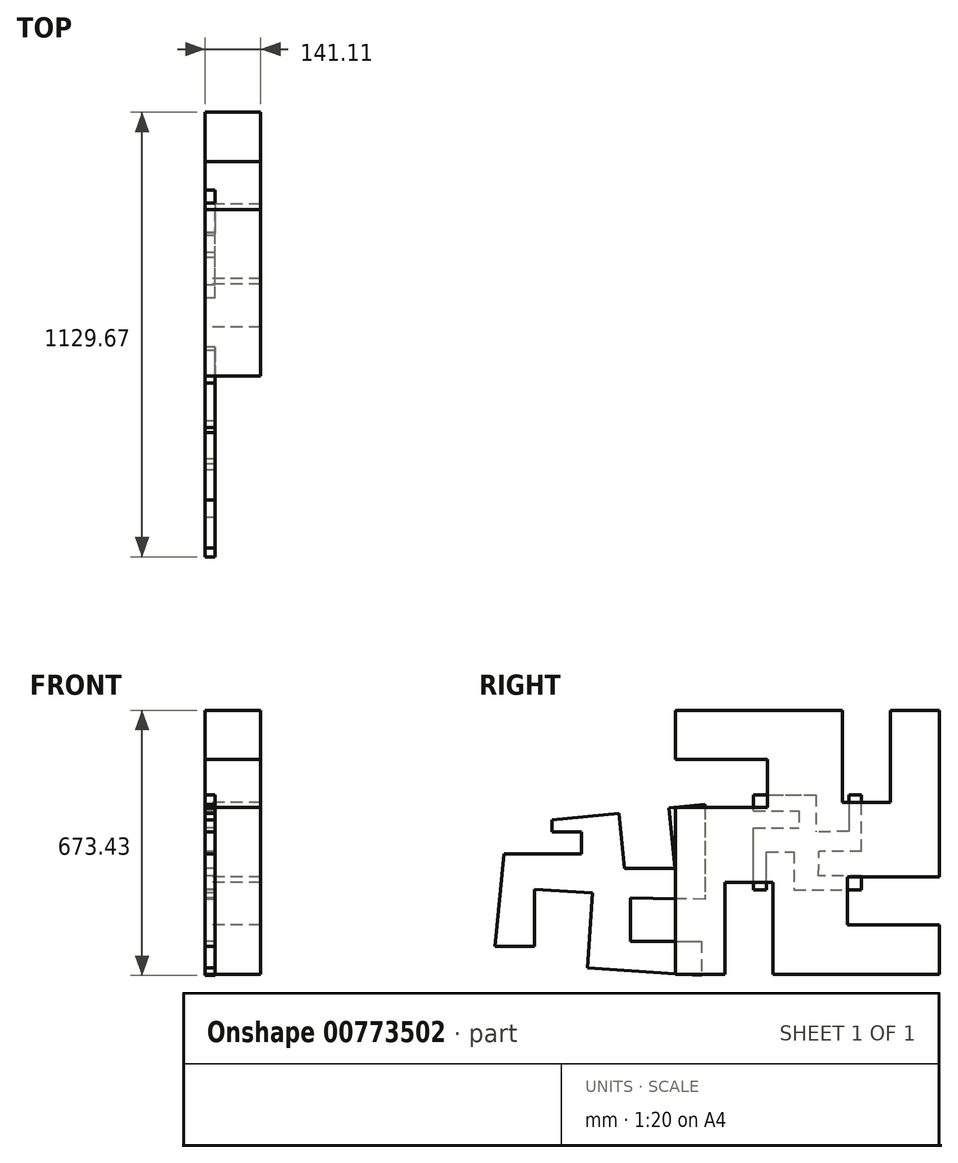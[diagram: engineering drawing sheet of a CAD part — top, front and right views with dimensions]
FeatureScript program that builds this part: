
annotation { "Feature Type Name" : "Feature", "Feature Type Description" : "" }
export const myFeature = defineFeature(function(context is Context, id is Id, definition is map)
    precondition{}
    {
        {
            var Q0;
            Q0=qCreatedBy(makeId("Right.planeOp"),FACE);
            var sketch = newSketch(context, id + "F0", { "sketchPlane" : qUnion([Q0])});
            skLineSegment(sketch, "E0.bottom", {"start": v(-137.35, -120.87) * mm, "end": v(137.35, -120.87) * mm});
            skLineSegment(sketch, "E0.top", {"start": v(-137.35, 120.87) * mm, "end": v(137.35, 120.87) * mm});
            skLineSegment(sketch, "E0.left", {"start": v(-137.35, -120.87) * mm, "end": v(-137.35, 120.87) * mm});
            skLineSegment(sketch, "E0.right", {"start": v(137.35, -120.87) * mm, "end": v(137.35, 120.87) * mm});
            skPoint(sketch, "E0.middle", {"position": v(0, 0) * mm});
            skLineSegment(sketch, "E1", {"start": v(-137.35, 79.77) * mm, "end": v(-21.68, 79.77) * mm});
            skLineSegment(sketch, "E2", {"start": v(21.28, 120.87) * mm, "end": v(21.28, 26.6) * mm});
            skLineSegment(sketch, "E3", {"start": v(104.57, 120.87) * mm, "end": v(104.57, 27.18) * mm});
            skLineSegment(sketch, "E4", {"start": v(104.57, 27.18) * mm, "end": v(21.28, 26.6) * mm});
            skLineSegment(sketch, "E5", {"start": v(137.35, -23.05) * mm, "end": v(28.75, -23.05) * mm});
            skLineSegment(sketch, "E6", {"start": v(137.35, -85.93) * mm, "end": v(28.16, -85.93) * mm});
            skLineSegment(sketch, "E7", {"start": v(28.16, -85.93) * mm, "end": v(28.75, -23.05) * mm});
            skLineSegment(sketch, "E8", {"start": v(-103.93, -120.87) * mm, "end": v(-103.93, -24.32) * mm});
            skLineSegment(sketch, "E9", {"start": v(-103.93, -24.32) * mm, "end": v(-34.55, -24.32) * mm});
            skLineSegment(sketch, "E10", {"start": v(-34.55, -24.32) * mm, "end": v(-34.55, -120.87) * mm});
            skLineSegment(sketch, "E11", {"start": v(-137.35, 36.22) * mm, "end": v(-21.68, 36.22) * mm});
            skLineSegment(sketch, "E12", {"start": v(-21.68, 79.77) * mm, "end": v(-21.68, 36.22) * mm});
            skPoint(sketch, "E13.orphan", {"position": v(-34.55, 0) * mm});
            skPoint(sketch, "E14.orphan", {"position": v(0, -23.05) * mm});
            skPoint(sketch, "E15.orphan", {"position": v(21.28, 0) * mm});
            skPoint(sketch, "E16.orphan", {"position": v(0, 36.22) * mm});
            skSolve(sketch);
        }
        {
            var Q0;
            Q0=qCreatedBy(makeId("Right.planeOp"),FACE);
            var sketch = newSketch(context, id + "F1", { "sketchPlane" : qUnion([Q0])});
            skLineSegment(sketch, "E17", {"start": v(-649.55, 56.86) * mm, "end": v(-479.05, 73.44) * mm});
            skLineSegment(sketch, "E18", {"start": v(-479.05, 73.44) * mm, "end": v(-465.44, -66.54) * mm});
            skLineSegment(sketch, "E19", {"start": v(-465.44, -66.54) * mm, "end": v(-337.42, -66.54) * mm});
            skLineSegment(sketch, "E20", {"start": v(-337.42, -66.54) * mm, "end": v(-352.75, 86.78) * mm});
            skLineSegment(sketch, "E21", {"start": v(-352.75, 86.78) * mm, "end": v(-261.3, 95.93) * mm});
            skLineSegment(sketch, "E22", {"start": v(-261.3, 95.93) * mm, "end": v(-261.3, -144.76) * mm});
            skLineSegment(sketch, "E23", {"start": v(-261.3, -144.76) * mm, "end": v(-450.04, -141.55) * mm});
            skLineSegment(sketch, "E24", {"start": v(-450.04, -141.55) * mm, "end": v(-450.04, -251.7) * mm});
            skLineSegment(sketch, "E25", {"start": v(-450.04, -251.7) * mm, "end": v(-270.06, -251.7) * mm});
            skLineSegment(sketch, "E26", {"start": v(-270.06, -251.7) * mm, "end": v(-270.06, -338.25) * mm});
            skLineSegment(sketch, "E27", {"start": v(-270.06, -338.25) * mm, "end": v(-558.74, -319.17) * mm});
            skLineSegment(sketch, "E28", {"start": v(-558.74, -319.17) * mm, "end": v(-546.17, -128.95) * mm});
            skLineSegment(sketch, "E29", {"start": v(-546.17, -128.95) * mm, "end": v(-694.07, -119.18) * mm});
            skLineSegment(sketch, "E30", {"start": v(-694.07, -119.18) * mm, "end": v(-694.07, -264.86) * mm});
            skLineSegment(sketch, "E31", {"start": v(-694.07, -264.86) * mm, "end": v(-794.49, -264.86) * mm});
            skLineSegment(sketch, "E32", {"start": v(-794.49, -264.86) * mm, "end": v(-771.64, -30.12) * mm});
            skLineSegment(sketch, "E33", {"start": v(-771.64, -30.12) * mm, "end": v(-573.77, -30.12) * mm});
            skLineSegment(sketch, "E34", {"start": v(-573.77, -30.12) * mm, "end": v(-573.77, 25.89) * mm});
            skLineSegment(sketch, "E35", {"start": v(-573.77, 25.89) * mm, "end": v(-649.55, 25.89) * mm});
            skLineSegment(sketch, "E36", {"start": v(-649.55, 25.89) * mm, "end": v(-649.55, 56.86) * mm});
            skSolve(sketch);
        }
        {
            var Q0;
            {var subQ0=sQuery(id+"F0.wireOp",EDGE,"E1");Q0=makeQuery(id+"F0.imprint","IMPRINT",FACE,{"disambiguationData":[TD([[makeQuery(id+"F0.imprint","IMPRINT",EDGE,{"derivedFrom":subQ0}),1.0]])]});}
            extrude(context, id + "F2", {"entities" : qUnion([Q0]), "depth" : 25.4 * mm, "offsetDistance" : 25.4 * mm});
        }
        {
            var Q0;
            Q0=makeQuery(id+"F1.imprint","IMPRINT",FACE,{"disambiguationData":[TD([[makeQuery(id+"F1.imprint","IMPRINT",EDGE,{"derivedFrom":sQuery(id+"F1.wireOp",EDGE,"E17")}),-1.0]])]});
            extrude(context, id + "F3", {"entities" : qUnion([Q0]), "depth" : 25.4 * mm, "offsetDistance" : 25.4 * mm});
        }
        {
            var Q0;
            Q0=qCreatedBy(makeId("Right.planeOp"),FACE);
            var sketch = newSketch(context, id + "F4", { "sketchPlane" : qUnion([Q0])});
            skLineSegment(sketch, "E37.bottom", {"start": v(-335.18, -335.18) * mm, "end": v(335.18, -335.18) * mm});
            skLineSegment(sketch, "E37.top", {"start": v(-335.18, 335.18) * mm, "end": v(335.18, 335.18) * mm});
            skLineSegment(sketch, "E37.left", {"start": v(-335.18, -335.18) * mm, "end": v(-335.18, 335.18) * mm});
            skLineSegment(sketch, "E37.right", {"start": v(335.18, -335.18) * mm, "end": v(335.18, 335.18) * mm});
            skPoint(sketch, "E37.middle", {"position": v(0, 0) * mm});
            skLineSegment(sketch, "E38", {"start": v(0, 0) * mm, "end": v(0, 335.18) * mm, "construction": true});
            skLineSegment(sketch, "E39", {"start": v(88.1, 335.18) * mm, "end": v(88.1, 101.7) * mm});
            skLineSegment(sketch, "E40", {"start": v(88.1, 101.7) * mm, "end": v(210.2, 101.7) * mm});
            skLineSegment(sketch, "E41", {"start": v(210.2, 101.7) * mm, "end": v(210.2, 335.18) * mm});
            skLineSegment(sketch, "E42.1.0", {"start": v(-101.7, 210.2) * mm, "end": v(-335.18, 210.2) * mm});
            skLineSegment(sketch, "E42.1.1", {"start": v(-101.7, 88.1) * mm, "end": v(-101.7, 210.2) * mm});
            skLineSegment(sketch, "E42.1.2", {"start": v(-335.18, 88.1) * mm, "end": v(-101.7, 88.1) * mm});
            skLineSegment(sketch, "E42.2.0", {"start": v(-210.2, -101.7) * mm, "end": v(-210.2, -335.18) * mm});
            skLineSegment(sketch, "E42.2.1", {"start": v(-88.1, -101.7) * mm, "end": v(-210.2, -101.7) * mm});
            skLineSegment(sketch, "E42.2.2", {"start": v(-88.1, -335.18) * mm, "end": v(-88.1, -101.7) * mm});
            skLineSegment(sketch, "E42.3.0", {"start": v(101.7, -210.2) * mm, "end": v(335.18, -210.2) * mm});
            skLineSegment(sketch, "E42.3.1", {"start": v(101.7, -88.1) * mm, "end": v(101.7, -210.2) * mm});
            skLineSegment(sketch, "E42.3.2", {"start": v(335.18, -88.1) * mm, "end": v(101.7, -88.1) * mm});
            skSolve(sketch);
        }
        {
            var Q0;
            {var subQ0=sQuery(id+"F4.wireOp",EDGE,"E39");Q0=makeQuery(id+"F4.imprint","IMPRINT",FACE,{"disambiguationData":[TD([[makeQuery(id+"F4.imprint","IMPRINT",EDGE,{"derivedFrom":subQ0}),-1.0]])]});}
            extrude(context, id + "F5", {"entities" : qUnion([Q0]), "depth" : 141.1 * mm, "offsetDistance" : 25.4 * mm});
        }
    });
